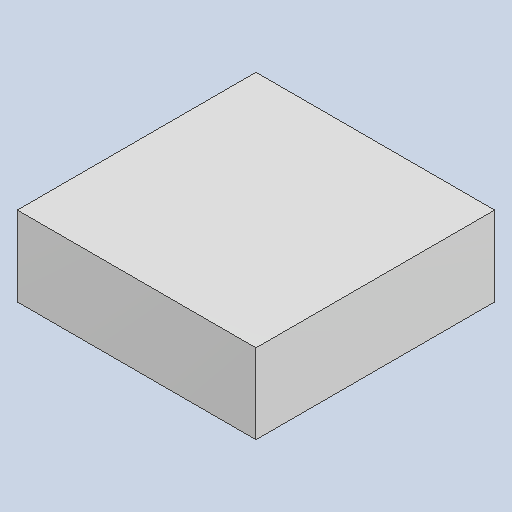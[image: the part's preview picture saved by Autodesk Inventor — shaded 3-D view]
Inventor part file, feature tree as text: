
AUTODESK INVENTOR PART (.ipt)
format: ipt  version: 2023.4 (Build 274418000, 418)  size: 79,872 bytes
history: native  units: mm
features: extrude x1
ambient origin geometry x8: Origin, YZ Plane, XZ Plane, XY Plane, X Axis, Y Axis, Z Axis, Center Point
bodies: Solid1 (feature_tree)
feature tree (1):
  extrude  "Extruded_8"  [1 undecoded]
note: 1 required parameter value undecoded (feature->parameter linkage not recoverable at this tier; creation-order binding heuristic only, values carry confidence <= 0.55)
